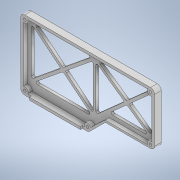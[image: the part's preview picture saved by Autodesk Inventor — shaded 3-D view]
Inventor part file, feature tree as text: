
AUTODESK INVENTOR PART (.ipt)
format: ipt  version: 2021 (Build 250183000, 183)  size: 492,544 bytes
history: native  units: mm
features: sketch x19, extrude x17, fillet x5, hole x2, chamfer x2
ambient origin geometry x8: Origin, YZ Plane, XZ Plane, XY Plane, X Axis, Y Axis, Z Axis, Center Point
bodies: Solid1 (feature_tree)
feature tree (45):
  extrude  "Extrusion1"  Depth=100.0mm
  extrude  "Extrusion2"  Depth=50.0mm
  hole  "Hole1"  [1 undecoded]
  extrude  "Extrusion3"  Depth=50.0mm
  extrude  "Extrusion4"  Depth=3.0mm
  extrude  "Extrusion5"  Depth=3.0mm
  fillet  "Fillet1"  Radius=49.0mm
  extrude  "Extrusion6"  Depth=49.0mm
  extrude  "Extrusion7"  Depth=5.0mm
  extrude  "Extrusion8"  Depth=5.0mm
  chamfer  "Chamfer1"  Distance=3.0mm
  extrude  "Extrusion9"  Depth=12.5mm
  fillet  "Fillet2"  Radius=63.1mm
  extrude  "Extrusion11"  Depth=3.0mm
  extrude  "Extrusion12"  Depth=2.0mm
  chamfer  "Chamfer2"  Distance=2.0mm
  extrude  "Extrusion13"  Depth=1.5mm
  extrude  "Extrusion14"  Depth=3.0mm TaperAngle=0.0deg
  extrude  "Extrusion15"  Depth=3.0mm
  fillet  "Fillet3"  Radius=7.6mm
  fillet  "Fillet4"  Radius=46.4mm
  hole  "Hole2"  [1 undecoded]
  extrude  "Extrusion20"  Depth=3.0mm TaperAngle=0.0deg
  extrude  "Extrusion21"  Depth=5.0mm
  fillet  "Fillet5"  Radius=2.0mm
  extrude  "Extrusion22"  Depth=12.0mm TaperAngle=0.0deg
  sketch  "Sketch1"  dims[d0=52.0mm d1=100.0mm]
  sketch  "Sketch2"  dims[d2=26.0mm d3=50.0mm]
  sketch  "Sketch3"  dims[d4=2.0mm d5=0.0mm d6=3.0mm]
  sketch  "Sketch4"  dims[d7=3.0mm d8=50.0mm]
  sketch  "Sketch5"  dims[d9=3.0mm d10=97.0mm]
  sketch  "Sketch6"  dims[d11=15.0mm d12=3.0mm d13=49.0mm]
  sketch  "Sketch7"  dims[d14=97.0mm d15=49.0mm]
  sketch  "Sketch8"  dims[d16=2.0mm d17=5.0mm]
  sketch  "Sketch9"  dims[d18=2.0mm d19=5.0mm]
  sketch  "Sketch10"  dims[d20=2.0mm]
  sketch  "Sketch12"  dims[d21=5.0mm]
  sketch  "Sketch13"  dims[d22=2.0mm]
  sketch  "Sketch14"  dims[d23=5.0mm]
  sketch  "Sketch15"  dims[d24=2.0mm]
  sketch  "Sketch16"  dims[d25=5.0mm d26=3.0mm d27=0.0mm]
  sketch  "Sketch17"  dims[d28=2.0mm d29=6.0mm d30=5.0mm d31=2.0mm d32=90.0deg d33=10.0mm d34=20.594885mm d35=12.5mm d36=63.1mm]
  sketch  "Sketch23"  dims[d37=3.0mm d38=0.0mm d39=50.673mm]
  sketch  "Sketch24"  dims[d40=3.0mm d41=0.0mm d42=2.0mm]
  sketch  "Sketch25"  dims[d43=2.0mm d44=2.0mm d45=1.5mm d46=3.0mm d47=0.0mm d48=3.0mm d49=7.6mm d50=46.4mm d51=6.7mm d52=3.0mm d53=0.0mm d54=5.0mm d55=2.0mm d56=12.0mm d57=0.0mm d58=1.4mm d59=1.2mm d60=3.0mm d61=14.0mm d62=1.2mm d63=1.4mm d64=12.0mm d65=3.0mm d66=0.0mm d67=1.0mm d68=2.0mm d69=45.0deg d70=1.2mm d71=3.0mm d72=0.0mm d73=1.0mm d77=3.0mm d78=0.0mm d79=3.0mm d80=3.0mm d81=3.0mm d82=3.0mm d83=3.0mm d84=3.0mm d85=3.0mm d86=48.0mm d87=2.0mm d88=0.0mm d89=8.4mm d90=2.0mm d91=45.0deg d92=1.2mm d93=3.0mm d94=0.0mm d95=7.6mm d96=5.0mm d97=0.0mm d98=2.0mm d99=2.0mm d100=2.0mm d101=2.0mm d102=2.0mm d103=2.0mm d104=0.0mm d105=1.0mm d106=1.0mm d107=2.0mm d108=6.0mm d109=5.0mm d110=2.0mm d111=90.0deg d112=4.0mm d113=20.594885mm d146=6.5mm d147=5.0mm d148=2.0mm d149=0.0mm d150=0.3mm d151=0.3mm d152=2.0mm d153=0.0mm d154=3.0mm d155=2.0mm d156=2.0mm d157=2.0mm d158=2.0mm d159=0.0mm d74=0.872665mm d75=0.872665mm d76=0.5mm d114=0.75mm d115=20.594885mm d116=0.0625mm d117=0.75mm d118=0.375mm]
note: 2 required parameter values undecoded (feature->parameter linkage not recoverable at this tier; creation-order binding heuristic only, values carry confidence <= 0.55)
